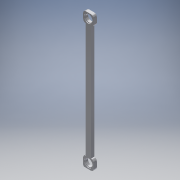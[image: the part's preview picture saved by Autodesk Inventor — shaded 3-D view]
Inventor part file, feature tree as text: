
AUTODESK INVENTOR PART (.ipt)
format: ipt  version: 2016 (Build 200138000, 138)  size: 154,112 bytes
history: native  units: mm (DEFAULTED — no unit token found)
features: extrude x3, fillet x2, sketch x1
ambient origin geometry x8: Origin, YZ Plane, XZ Plane, XY Plane, X Axis, Y Axis, Z Axis, Center Point
bodies: Solid1 (feature_tree)
feature tree (6):
  extrude  "Extrusion1"  Depth=330.2mm
  extrude  "Extrusion2"  Depth=6.35mm
  extrude  "Extrusion5"  Depth=12.7mm
  fillet  "Fillet1"  Radius=7.9375mm
  fillet  "Fillet2"  Radius=25.4mm
  sketch  "Sketch2"  dims[d0=25.4mm d1=330.2mm d2=17.4625mm d3=12.7mm d4=7.9375mm d5=0.0mm d8=25.4mm d9=0.0mm d14=20.6375mm d17=1.5875mm d18=0.0mm d38=6.35mm d39=3.175mm d40=17.4625mm d41=12.7mm d42=12.7mm d45=279.4mm d46=25.4mm d47=6.35mm d48=279.4mm d49=25.4mm d50=6.35mm d51=20.6375mm]
